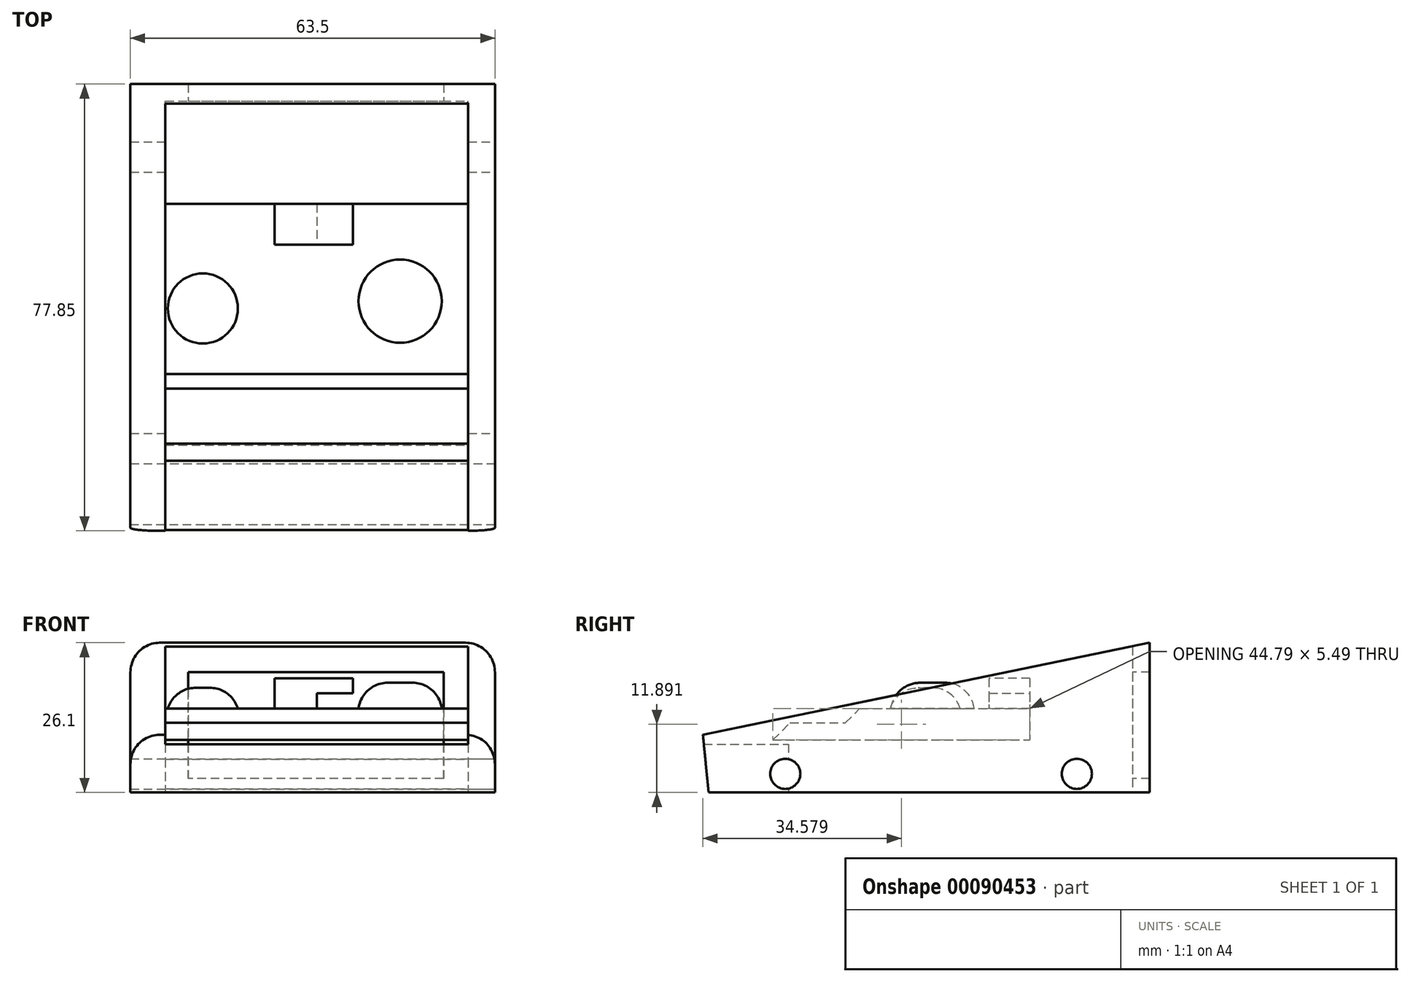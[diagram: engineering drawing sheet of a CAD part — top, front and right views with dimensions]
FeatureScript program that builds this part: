
annotation { "Feature Type Name" : "Feature", "Feature Type Description" : "" }
export const myFeature = defineFeature(function(context is Context, id is Id, definition is map)
    precondition{}
    {
        {
            var Q0;
            Q0=qCreatedBy(makeId("Right.planeOp"),FACE);
            var sketch = newSketch(context, id + "F0", { "sketchPlane" : qUnion([Q0])});
            skLineSegment(sketch, "E0", {"start": v(-71.02, 0) * mm, "end": v(55.62, 26.1) * mm});
            skLineSegment(sketch, "E1", {"start": v(55.62, 26.1) * mm, "end": v(55.62, 0) * mm});
            skLineSegment(sketch, "E2", {"start": v(55.62, 0) * mm, "end": v(-71.02, 0) * mm});
            skSolve(sketch);
        }
        {
            var Q0;
            Q0 = qSketchRegion(id + "F0", true);
            extrude(context, id + "F1", {"entities" : qUnion([Q0]), "endBound" : BoundingType.SYMMETRIC, "depth" : 63.5 * mm});
        }
        {
            var Q0;
            Q0=makeQuery(id+"F1.opExtrude","SWEPT_FACE",FACE,{"disambiguationData":[OSD([sQuery(id+"F0.wireOp",EDGE,"E2")])]});
            var sketch = newSketch(context, id + "F2", { "sketchPlane" : qUnion([Q0])});
            skLineSegment(sketch, "E3.bottom", {"start": v(-25.67, 68.03) * mm, "end": v(27.1, 68.03) * mm});
            skLineSegment(sketch, "E3.top", {"start": v(-25.67, -52.63) * mm, "end": v(27.1, -52.63) * mm});
            skLineSegment(sketch, "E3.left", {"start": v(-25.67, 68.03) * mm, "end": v(-25.67, -52.63) * mm});
            skLineSegment(sketch, "E3.right", {"start": v(27.1, 68.03) * mm, "end": v(27.1, -52.63) * mm});
            skSolve(sketch);
        }
        {
            var Q0;
            Q0=makeQuery(id+"F2.imprint","IMPRINT",FACE,{"disambiguationData":[TD([[makeQuery(id+"F2.imprint","IMPRINT",EDGE,{"derivedFrom":sQuery(id+"F2.wireOp",EDGE,"E3.bottom")}),-1.0]])]});
            extrude(context, id + "F3", {"entities" : qUnion([Q0]), "operationType" : NewBodyOperationType.REMOVE, "oppositeDirection" : true, "depth" : 25.4 * mm});
        }
        {
            var Q0;
            Q0=makeQuery(id+"F3.boolean.opBoolean","COPY",FACE,{"derivedFrom":makeQuery(id+"F3.opExtrude","SWEPT_FACE",FACE,{"disambiguationData":[OSD([sQuery(id+"F2.wireOp",EDGE,"E3.top")])]})});
            var sketch = newSketch(context, id + "F4", { "sketchPlane" : qUnion([Q0])});
            skLineSegment(sketch, "E4.bottom", {"start": v(-21.68, 20.97) * mm, "end": v(22.82, 20.97) * mm});
            skLineSegment(sketch, "E4.top", {"start": v(-21.68, 2.42) * mm, "end": v(22.82, 2.42) * mm});
            skLineSegment(sketch, "E4.left", {"start": v(-21.68, 20.97) * mm, "end": v(-21.68, 2.42) * mm});
            skLineSegment(sketch, "E4.right", {"start": v(22.82, 20.97) * mm, "end": v(22.82, 2.42) * mm});
            skSolve(sketch);
        }
        {
            var Q0;
            Q0=makeQuery(id+"F4.imprint","IMPRINT",FACE,{"disambiguationData":[TD([[makeQuery(id+"F4.imprint","IMPRINT",EDGE,{"derivedFrom":sQuery(id+"F4.wireOp",EDGE,"E4.bottom")}),-1.0]])]});
            extrude(context, id + "F5", {"entities" : qUnion([Q0]), "operationType" : NewBodyOperationType.REMOVE, "oppositeDirection" : true, "depth" : 25.4 * mm});
        }
        {
            var Q0;
            Q0=makeQuery(id+"F3.boolean.opBoolean","COPY",FACE,{"derivedFrom":makeQuery(id+"F3.opExtrude","SWEPT_FACE",FACE,{"disambiguationData":[OSD([sQuery(id+"F2.wireOp",EDGE,"E3.left")])]})});
            var sketch = newSketch(context, id + "F6", { "sketchPlane" : qUnion([Q0])});
            skLineSegment(sketch, "E5.bottom", {"start": v(0, 14.64) * mm, "end": v(34.74, 14.64) * mm});
            skLineSegment(sketch, "E5.top", {"start": v(0, 9.15) * mm, "end": v(34.74, 9.15) * mm});
            skLineSegment(sketch, "E5.left", {"start": v(0, 14.64) * mm, "end": v(0, 9.15) * mm});
            skLineSegment(sketch, "E5.right", {"start": v(34.74, 14.64) * mm, "end": v(34.74, 9.15) * mm});
            skSolve(sketch);
        }
        {
            var Q0;
            Q0=makeQuery(id+"F6.imprint","IMPRINT",FACE,{"disambiguationData":[TD([[makeQuery(id+"F6.imprint","IMPRINT",EDGE,{"derivedFrom":sQuery(id+"F6.wireOp",EDGE,"E5.bottom")}),-1.0]])]});
            extrude(context, id + "F7", {"entities" : qUnion([Q0]), "operationType" : NewBodyOperationType.ADD, "depth" : 54.31 * mm});
        }
        {
            var Q0;
            Q0=makeQuery(id+"F3.boolean.opBoolean","COPY",FACE,{"derivedFrom":makeQuery(id+"F3.opExtrude","SWEPT_FACE",FACE,{"disambiguationData":[OSD([sQuery(id+"F2.wireOp",EDGE,"E3.left")])]})});
            var sketch = newSketch(context, id + "F8", { "sketchPlane" : qUnion([Q0])});
            skLineSegment(sketch, "E6.bottom", {"start": v(-12.14, 12.14) * mm, "end": v(6.47, 12.14) * mm});
            skLineSegment(sketch, "E6.top", {"start": v(-12.14, 9.15) * mm, "end": v(6.47, 9.15) * mm});
            skLineSegment(sketch, "E6.left", {"start": v(-12.14, 12.14) * mm, "end": v(-12.14, 9.15) * mm});
            skLineSegment(sketch, "E6.right", {"start": v(6.47, 12.14) * mm, "end": v(6.47, 9.15) * mm});
            skSolve(sketch);
        }
        {
            var Q0;
            {var subQ0=sQuery(id+"F8.wireOp",EDGE,"E6.left");Q0=makeQuery(id+"F8.imprint","IMPRINT",FACE,{"disambiguationData":[TD([[makeQuery(id+"F8.imprint","IMPRINT",EDGE,{"derivedFrom":subQ0}),1.0]])]});}
            extrude(context, id + "F9", {"entities" : qUnion([Q0]), "operationType" : NewBodyOperationType.ADD, "depth" : 56.7 * mm});
        }
        {
            var Q0;
            {var subQ0=sQuery(id+"F2.wireOp",EDGE,"E3.left");var subQ1=makeQuery(id+"F3.boolean.opBoolean","COPY",FACE,{"derivedFrom":makeQuery(id+"F3.opExtrude","SWEPT_FACE",FACE,{"disambiguationData":[OSD([subQ0])]})});var subQ2=sQuery(id+"F2.wireOp",EDGE,"E3.top");var subQ3=sQuery(id+"F2.wireOp",EDGE,"E3.bottom");Q0=makeQuery(id+"F9.boolean.opBoolean","SPLIT",FACE,{"disambiguationData":[TD([makeQuery(id+"F1.opExtrude","SWEPT_FACE",FACE,{"disambiguationData":[OSD([sQuery(id+"F0.wireOp",EDGE,"E0")])]}),makeQuery(id+"F1.opExtrude","SWEPT_FACE",FACE,{"disambiguationData":[OSD([sQuery(id+"F0.wireOp",EDGE,"E2")])]}),makeQuery(id+"F3.boolean.opBoolean","COPY",FACE,{"derivedFrom":makeQuery(id+"F3.opExtrude","SWEPT_FACE",FACE,{"disambiguationData":[OSD([subQ3])]})}),makeQuery(id+"F3.boolean.opBoolean","COPY",FACE,{"derivedFrom":makeQuery(id+"F3.opExtrude","CAP_FACE",FACE,{"disambiguationData":[OSD([subQ3,subQ2,subQ0,sQuery(id+"F2.wireOp",EDGE,"E3.right")])],"isStart":false})}),makeQuery(id+"F3.boolean.opBoolean","COPY",FACE,{"derivedFrom":makeQuery(id+"F3.opExtrude","SWEPT_FACE",FACE,{"disambiguationData":[OSD([subQ2])]})}),subQ1,makeQuery(id+"F7.opExtrude","SWEPT_FACE",FACE,{"disambiguationData":[OSD([sQuery(id+"F6.wireOp",EDGE,"E5.bottom")])]}),makeQuery(id+"F7.opExtrude","SWEPT_FACE",FACE,{"disambiguationData":[OSD([sQuery(id+"F6.wireOp",EDGE,"E5.top")])]}),makeQuery(id+"F7.opExtrude","SWEPT_FACE",FACE,{"disambiguationData":[OSD([sQuery(id+"F6.wireOp",EDGE,"E5.left")])]}),makeQuery(id+"F7.opExtrude","SWEPT_FACE",FACE,{"disambiguationData":[OSD([sQuery(id+"F6.wireOp",EDGE,"E5.right")])]}),makeQuery(id+"F9.opExtrude","SWEPT_FACE",FACE,{"disambiguationData":[OSD([sQuery(id+"F8.wireOp",EDGE,"E6.bottom")])]}),makeQuery(id+"F9.opExtrude","SWEPT_FACE",FACE,{"disambiguationData":[OSD([sQuery(id+"F8.wireOp",EDGE,"E6.top")])]}),makeQuery(id+"F9.opExtrude","SWEPT_FACE",FACE,{"disambiguationData":[OSD([sQuery(id+"F8.wireOp",EDGE,"E6.left")])]})])],"derivedFrom":subQ1});}
            var sketch = newSketch(context, id + "F10", { "sketchPlane" : qUnion([Q0])});
            skLineSegment(sketch, "E7.bottom", {"start": v(-30.1, 8.43) * mm, "end": v(-7.31, 8.43) * mm});
            skLineSegment(sketch, "E7.top", {"start": v(-30.1, 0) * mm, "end": v(-7.31, 0) * mm});
            skLineSegment(sketch, "E7.left", {"start": v(-30.1, 8.43) * mm, "end": v(-30.1, 0) * mm});
            skLineSegment(sketch, "E7.right", {"start": v(-7.31, 8.43) * mm, "end": v(-7.31, 0) * mm});
            skSolve(sketch);
        }
        {
            var Q0;
            Q0=makeQuery(id+"F10.imprint","IMPRINT",FACE,{"disambiguationData":[TD([[makeQuery(id+"F10.imprint","IMPRINT",EDGE,{"derivedFrom":sQuery(id+"F10.wireOp",EDGE,"E7.bottom")}),-1.0]])]});
            extrude(context, id + "F11", {"entities" : qUnion([Q0]), "operationType" : NewBodyOperationType.ADD, "depth" : 56.07 * mm});
        }
        {
            var Q0;
            Q0=makeQuery(id+"F7.opExtrude","SWEPT_EDGE",EDGE,{"disambiguationData":[OSD([sQuery(id+"F0.wireOp",EDGE,"E0"),sQuery(id+"F2.wireOp",EDGE,"E3.left"),sQuery(id+"F6.wireOp",EDGE,"E5.bottom"),sQuery(id+"F6.wireOp",EDGE,"E5.left")])]});
            var Q1;
            Q1=makeQuery(id+"F9.opExtrude","SWEPT_EDGE",EDGE,{"disambiguationData":[OSD([sQuery(id+"F0.wireOp",EDGE,"E0"),sQuery(id+"F2.wireOp",EDGE,"E3.left"),sQuery(id+"F8.wireOp",EDGE,"E6.bottom"),sQuery(id+"F8.wireOp",EDGE,"E6.left")])]});
            var Q2;
            Q2=makeQuery(id+"F11.opExtrude","SWEPT_EDGE",EDGE,{"disambiguationData":[OSD([sQuery(id+"F0.wireOp",EDGE,"E0"),sQuery(id+"F2.wireOp",EDGE,"E3.left"),sQuery(id+"F10.wireOp",EDGE,"E7.bottom"),sQuery(id+"F10.wireOp",EDGE,"E7.left")])]});
            chamfer(context, id + "F12", {"entities" : qUnion([Q0, Q1, Q2]), "width" : 5.08 * mm, "tangentPropagation" : true});
        }
        {
            var Q0;
            {var subQ0=makeQuery(id+"F7.opExtrude","SWEPT_FACE",FACE,{"disambiguationData":[OSD([sQuery(id+"F6.wireOp",EDGE,"E5.right")])]});var subQ1=makeQuery(id+"F7.opExtrude","SWEPT_FACE",FACE,{"disambiguationData":[OSD([sQuery(id+"F6.wireOp",EDGE,"E5.left")])]});var subQ2=makeQuery(id+"F7.opExtrude","SWEPT_FACE",FACE,{"disambiguationData":[OSD([sQuery(id+"F6.wireOp",EDGE,"E5.bottom")])]});var subQ3=sQuery(id+"F2.wireOp",EDGE,"E3.left");var subQ4=makeQuery(id+"F3.boolean.opBoolean","COPY",FACE,{"derivedFrom":makeQuery(id+"F3.opExtrude","SWEPT_FACE",FACE,{"disambiguationData":[OSD([subQ3])]})});var subQ5=makeQuery(id+"F1.opExtrude","SWEPT_FACE",FACE,{"disambiguationData":[OSD([sQuery(id+"F0.wireOp",EDGE,"E0")])]});var subQ6=makeQuery(id+"F9.opExtrude","SWEPT_FACE",FACE,{"disambiguationData":[OSD([sQuery(id+"F8.wireOp",EDGE,"E6.bottom")])]});var subQ8=makeQuery(id+"F1.opExtrude","SWEPT_FACE",FACE,{"disambiguationData":[OSD([sQuery(id+"F0.wireOp",EDGE,"E2")])]});var subQ9=sQuery(id+"F2.wireOp",EDGE,"E3.top");var subQ10=sQuery(id+"F2.wireOp",EDGE,"E3.bottom");var subQ11=makeQuery(id+"F3.boolean.opBoolean","COPY",FACE,{"derivedFrom":makeQuery(id+"F3.opExtrude","CAP_FACE",FACE,{"disambiguationData":[OSD([subQ10,subQ9,subQ3,sQuery(id+"F2.wireOp",EDGE,"E3.right")])],"isStart":false})});var subQ12=makeQuery(id+"F7.opExtrude","SWEPT_FACE",FACE,{"disambiguationData":[OSD([sQuery(id+"F6.wireOp",EDGE,"E5.top")])]});var subQ13=makeQuery(id+"F3.boolean.opBoolean","COPY",FACE,{"derivedFrom":makeQuery(id+"F3.opExtrude","SWEPT_FACE",FACE,{"disambiguationData":[OSD([subQ9])]})});var subQ14=makeQuery(id+"F9.opExtrude","SWEPT_FACE",FACE,{"disambiguationData":[OSD([sQuery(id+"F8.wireOp",EDGE,"E6.top")])]});var subQ15=makeQuery(id+"F9.opExtrude","SWEPT_FACE",FACE,{"disambiguationData":[OSD([sQuery(id+"F8.wireOp",EDGE,"E6.left")])]});var subQ18=makeQuery(id+"F3.boolean.opBoolean","COPY",FACE,{"derivedFrom":makeQuery(id+"F3.opExtrude","SWEPT_FACE",FACE,{"disambiguationData":[OSD([subQ10])]})});var subQ19=subQ4;var subQ20=makeQuery(id+"F9.boolean.opBoolean","SPLIT",FACE,{"disambiguationData":[TD([subQ5,subQ8,subQ18,subQ11,subQ13,subQ4,subQ2,subQ12,subQ1,subQ0,subQ6,subQ14,subQ15])],"derivedFrom":subQ19});Q0=makeQuery(id+"F12.opChamfer","MERGE",FACE,{"derivedFrom":[makeQuery(id+"F9.boolean.opBoolean","SPLIT",FACE,{"disambiguationData":[TD([subQ5,subQ4,subQ2,subQ1,subQ6,subQ15])],"derivedFrom":subQ19}),makeQuery(id+"F11.boolean.opBoolean","SPLIT",FACE,{"disambiguationData":[TD([subQ18])],"derivedFrom":subQ20}),makeQuery(id+"F11.boolean.opBoolean","SPLIT",FACE,{"disambiguationData":[TD([subQ13])],"derivedFrom":subQ20})]});}
            var sketch = newSketch(context, id + "F13", { "sketchPlane" : qUnion([Q0])});
            skLineSegment(sketch, "E8.bottom", {"start": v(-44, 0) * mm, "end": v(-68.03, 0) * mm});
            skLineSegment(sketch, "E8.top", {"start": v(-44, 3.49) * mm, "end": v(-68.03, 3.49) * mm});
            skLineSegment(sketch, "E8.left", {"start": v(-44, 0) * mm, "end": v(-44, 3.49) * mm});
            skLineSegment(sketch, "E8.right", {"start": v(-68.03, 0) * mm, "end": v(-68.03, 3.49) * mm});
            skSolve(sketch);
        }
        {
            var Q0;
            {var subQ1=sQuery(id+"F13.wireOp",EDGE,"E8.bottom");Q0=makeQuery(id+"F13.imprint","IMPRINT",FACE,{"disambiguationData":[TD([[makeQuery(id+"F13.imprint","IMPRINT",EDGE,{"derivedFrom":subQ1}),1.0]])]});}
            extrude(context, id + "F14", {"entities" : qUnion([Q0]), "operationType" : NewBodyOperationType.ADD, "depth" : 55.98 * mm});
        }
        {
            var Q0;
            Q0=makeQuery(id+"F14.opExtrude","SWEPT_EDGE",EDGE,{"disambiguationData":[OSD([sQuery(id+"F0.wireOp",EDGE,"E0"),sQuery(id+"F2.wireOp",EDGE,"E3.left"),sQuery(id+"F13.wireOp",EDGE,"E8.top")])]});
            chamfer(context, id + "F15", {"entities" : qUnion([Q0]), "width" : 5.08 * mm, "tangentPropagation" : true});
        }
        {
            var Q0;
            Q0=makeQuery(id+"F7.opExtrude","SWEPT_FACE",FACE,{"disambiguationData":[OSD([sQuery(id+"F6.wireOp",EDGE,"E5.bottom")])]});
            var sketch = newSketch(context, id + "F16", { "sketchPlane" : qUnion([Q0])});
            skCircle(sketch, "E9", {"center": v(15.24, 17.79) * mm, "radius": 7.25 * mm});
            skSolve(sketch);
        }
        {
            var Q0;
            Q0=makeQuery(id+"F16.imprint","IMPRINT",FACE,{"disambiguationData":[TD([[makeQuery(id+"F16.imprint","IMPRINT",EDGE,{"derivedFrom":sQuery(id+"F16.wireOp",EDGE,"E9")}),1.0]])]});
            extrude(context, id + "F17", {"entities" : qUnion([Q0]), "operationType" : NewBodyOperationType.ADD, "depth" : 4.48 * mm});
        }
        {
            var Q0;
            Q0=makeQuery(id+"F17.opExtrude","CAP_EDGE",EDGE,{"disambiguationData":[OSD([sQuery(id+"F16.wireOp",EDGE,"E9")])],"isStart":false});
            fillet(context, id + "F18", {"entities" : qUnion([Q0]), "radius" : 5.08 * mm, "tangentPropagation" : true, "allowEdgeOverflow" : false});
        }
        {
            var Q0;
            Q0=makeQuery(id+"F1.opExtrude","SWEPT_EDGE",EDGE,{"disambiguationData":[OSD([sQuery(id+"F0.wireOp",EDGE,"E0"),sQuery(id+"F0.wireOp",EDGE,"E2")])]});
            chamfer(context, id + "F19", {"entities" : qUnion([Q0]), "width" : 5.08 * mm, "tangentPropagation" : true});
        }
        {
            var Q0;
            Q0=makeQuery(id+"F1.opExtrude","CAP_EDGE",EDGE,{"disambiguationData":[OSD([sQuery(id+"F0.wireOp",EDGE,"E0")])],"isStart":true});
            var Q1;
            Q1=makeQuery(id+"F1.opExtrude","CAP_EDGE",EDGE,{"disambiguationData":[OSD([sQuery(id+"F0.wireOp",EDGE,"E0")])],"isStart":false});
            fillet(context, id + "F20", {"entities" : qUnion([Q0, Q1]), "radius" : 5.08 * mm, "tangentPropagation" : true, "allowEdgeOverflow" : false});
        }
        {
            var Q0;
            Q0=makeQuery(id+"F7.opExtrude","SWEPT_FACE",FACE,{"disambiguationData":[OSD([sQuery(id+"F6.wireOp",EDGE,"E5.bottom")])]});
            var sketch = newSketch(context, id + "F21", { "sketchPlane" : qUnion([Q0])});
            skCircle(sketch, "E10", {"center": v(-19.14, 16.51) * mm, "radius": 6.1 * mm});
            skSolve(sketch);
        }
        {
            var Q0;
            Q0=makeQuery(id+"F21.imprint","IMPRINT",FACE,{"disambiguationData":[TD([[makeQuery(id+"F21.imprint","IMPRINT",EDGE,{"derivedFrom":sQuery(id+"F21.wireOp",EDGE,"E10")}),1.0]])]});
            extrude(context, id + "F22", {"entities" : qUnion([Q0]), "operationType" : NewBodyOperationType.ADD, "depth" : 3.6 * mm});
        }
        {
            var Q0;
            Q0=makeQuery(id+"F22.opExtrude","CAP_EDGE",EDGE,{"disambiguationData":[OSD([sQuery(id+"F21.wireOp",EDGE,"E10")])],"isStart":false});
            fillet(context, id + "F23", {"entities" : qUnion([Q0]), "radius" : 5.08 * mm, "tangentPropagation" : true, "allowEdgeOverflow" : false});
        }
        {
            var Q0;
            Q0=makeQuery(id+"F1.opExtrude","CAP_FACE",FACE,{"disambiguationData":[OSD([sQuery(id+"F0.wireOp",EDGE,"E0"),sQuery(id+"F0.wireOp",EDGE,"E1"),sQuery(id+"F0.wireOp",EDGE,"E2")])],"isStart":false});
            var sketch = newSketch(context, id + "F24", { "sketchPlane" : qUnion([Q0])});
            skCircle(sketch, "E11", {"center": v(-7.88, 3.25) * mm, "radius": 2.63 * mm});
            skCircle(sketch, "E12", {"center": v(42.92, 3.25) * mm, "radius": 2.63 * mm});
            skLineSegment(sketch, "E13", {"start": v(42.92, 3.25) * mm, "end": v(-7.88, 3.25) * mm, "construction": true});
            skSolve(sketch);
        }
        {
            var Q0;
            Q0=makeQuery(id+"F24.imprint","IMPRINT",FACE,{"disambiguationData":[TD([[makeQuery(id+"F24.imprint","IMPRINT",EDGE,{"derivedFrom":sQuery(id+"F24.wireOp",EDGE,"E11")}),1.0]])]});
            extrude(context, id + "F25", {"entities" : qUnion([Q0]), "operationType" : NewBodyOperationType.REMOVE, "oppositeDirection" : true, "depth" : 82.93 * mm});
        }
        {
            var Q0;
            Q0 = qSketchRegion(id + "F24", true);
            extrude(context, id + "F26", {"entities" : qUnion([Q0]), "operationType" : NewBodyOperationType.REMOVE, "endBound" : BoundingType.SYMMETRIC, "oppositeDirection" : true, "depth" : 192.22 * mm});
        }
        {
            var Q0;
            Q0=makeQuery(id+"F7.opExtrude","SWEPT_FACE",FACE,{"disambiguationData":[OSD([sQuery(id+"F6.wireOp",EDGE,"E5.bottom")])]});
            var sketch = newSketch(context, id + "F27", { "sketchPlane" : qUnion([Q0])});
            skPoint(sketch, "E14.oppositeSnap0", {"position": v(0.71, 34.74) * mm});
            skLineSegment(sketch, "E14.bottom", {"start": v(-6.64, 34.74) * mm, "end": v(0.71, 34.74) * mm});
            skLineSegment(sketch, "E14.top", {"start": v(-6.64, 27.6) * mm, "end": v(0.71, 27.6) * mm});
            skLineSegment(sketch, "E14.left", {"start": v(-6.64, 34.74) * mm, "end": v(-6.64, 27.6) * mm});
            skLineSegment(sketch, "E14.right", {"start": v(0.71, 34.74) * mm, "end": v(0.71, 27.6) * mm});
            skSolve(sketch);
        }
        {
            var Q0;
            Q0=makeQuery(id+"F27.imprint","IMPRINT",FACE,{"disambiguationData":[TD([[makeQuery(id+"F27.imprint","IMPRINT",EDGE,{"derivedFrom":sQuery(id+"F27.wireOp",EDGE,"E14.bottom")}),1.0]])]});
            extrude(context, id + "F28", {"entities" : qUnion([Q0]), "operationType" : NewBodyOperationType.ADD, "depth" : 1.8 * mm});
        }
        {
            var Q0;
            Q0=makeQuery(id+"F28.opExtrude","CAP_FACE",FACE,{"disambiguationData":[OSD([sQuery(id+"F27.wireOp",EDGE,"E14.bottom"),sQuery(id+"F27.wireOp",EDGE,"E14.top"),sQuery(id+"F27.wireOp",EDGE,"E14.left"),sQuery(id+"F27.wireOp",EDGE,"E14.right")])],"isStart":false});
            extrude(context, id + "F29", {"entities" : qUnion([Q0]), "operationType" : NewBodyOperationType.ADD, "depth" : 3.46 * mm});
        }
        {
            var Q0;
            {var subQ0=sQuery(id+"F27.wireOp",EDGE,"E14.right");Q0=makeQuery(id+"F29.boolean.opBoolean","MERGE",FACE,{"derivedFrom":[makeQuery(id+"F28.opExtrude","SWEPT_FACE",FACE,{"disambiguationData":[OSD([subQ0])]}),makeQuery(id+"F29.opExtrude","SWEPT_FACE",FACE,{"disambiguationData":[OSD([subQ0])]})]});}
            var sketch = newSketch(context, id + "F30", { "sketchPlane" : qUnion([Q0])});
            skLineSegment(sketch, "E15.bottom", {"start": v(27.6, 19.9) * mm, "end": v(34.74, 19.9) * mm});
            skLineSegment(sketch, "E15.top", {"start": v(27.6, 17.27) * mm, "end": v(34.74, 17.27) * mm});
            skLineSegment(sketch, "E15.left", {"start": v(27.6, 19.9) * mm, "end": v(27.6, 17.27) * mm});
            skLineSegment(sketch, "E15.right", {"start": v(34.74, 19.9) * mm, "end": v(34.74, 17.27) * mm});
            skSolve(sketch);
        }
        {
            var Q0;
            Q0=makeQuery(id+"F30.imprint","IMPRINT",FACE,{"disambiguationData":[TD([[makeQuery(id+"F30.imprint","IMPRINT",EDGE,{"derivedFrom":sQuery(id+"F30.wireOp",EDGE,"E15.bottom")}),1.0]])]});
            extrude(context, id + "F31", {"entities" : qUnion([Q0]), "operationType" : NewBodyOperationType.ADD, "depth" : 6.3 * mm});
        }
    });
